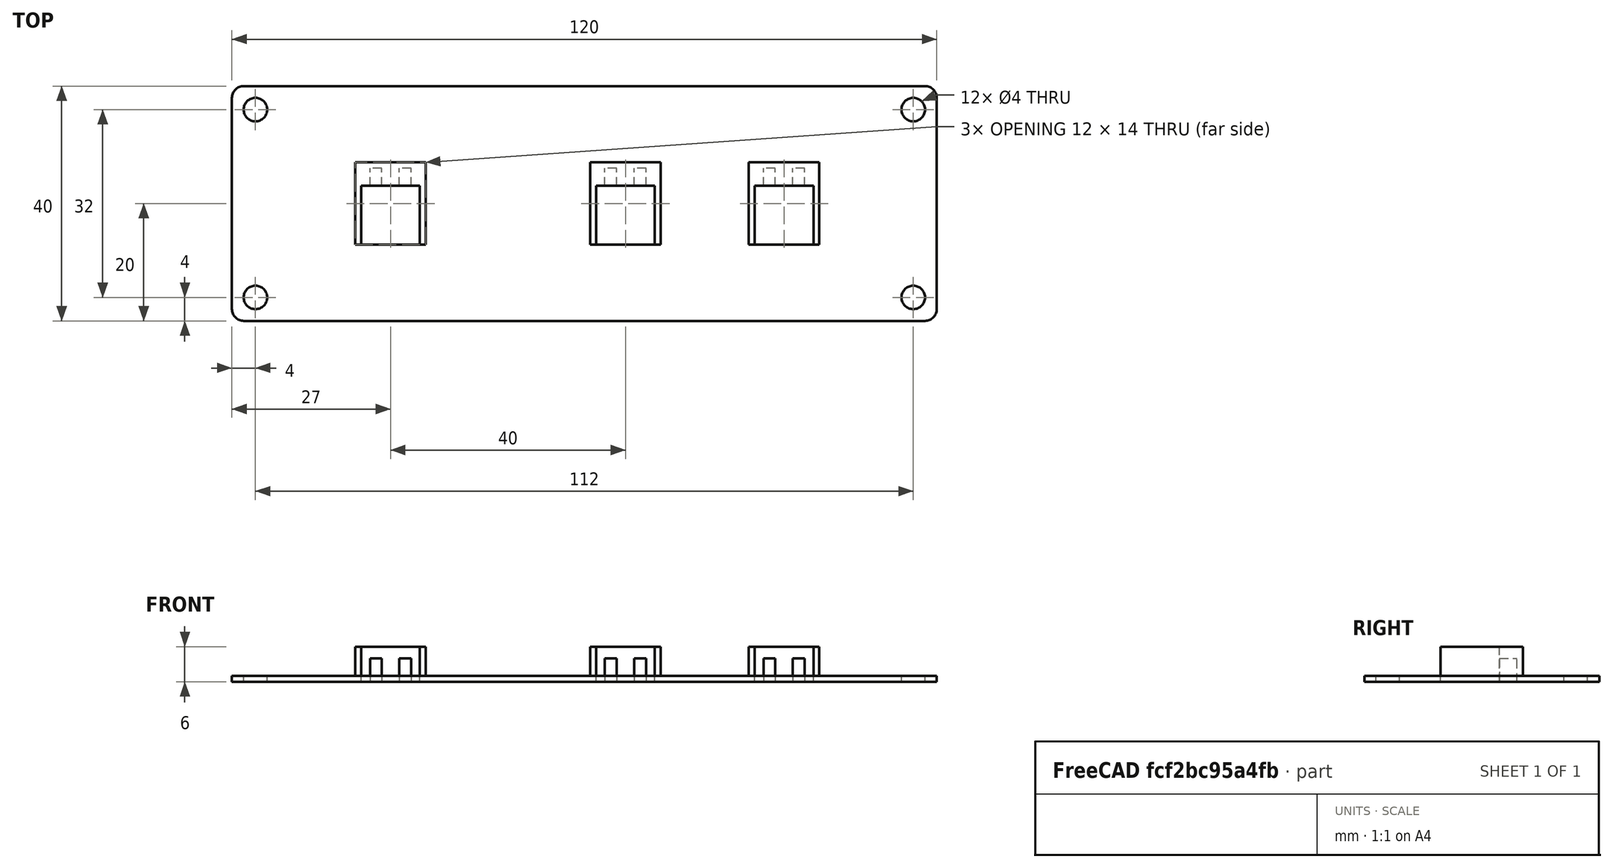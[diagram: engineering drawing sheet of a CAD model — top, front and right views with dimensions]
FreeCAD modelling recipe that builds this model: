
FCSTD DOCUMENT  (FreeCAD 0.18.4R)
Label: Parte_trasera
License: All rights reserved
LicenseURL: http://en.wikipedia.org/wiki/All_rights_reserved
objects: Part::Box×13, Part::MultiFuse×6, Part::Cut×2, Part::Feature×2, Part::Cylinder×1, Part::FeaturePython×1, Part::Fillet×1
note: 26 computed .brp shape members not serialized (recipe doc carries the construction recipe); baked Part::Feature solids carry a one-line shape summary decoded from their .brp

FEATURE [Part::Box] Box  label="Cubo"
  AttacherType = Attacher::AttachEngine3D
  Height = 1
  Length = 120
  Width = 40
FEATURE [Part::Cylinder] Cylinder  label="Cilindro"
  Angle = 360
  AttacherType = Attacher::AttachEngine3D
  Height = 10
  Placement = pos=(4,4,-1) rot=(0,0,1;0rad)
  Radius = 2
FEATURE [Part::FeaturePython] Array  # Draft array (typed FeaturePython)
  Angle = 360
  ArrayType = 0
  Axis = (0,0,1)
  Base = -> Cylinder
  Center = (0,0,0)
  Fuse = false
  IntervalAxis = (0,0,0)
  IntervalX = (112,0,0)
  IntervalY = (0,32,0)
  IntervalZ = (0,0,1)
  NumberPolar = 1
  NumberX = 2
  NumberY = 2
  NumberZ = 1
FEATURE [Part::Cut] Cut
  Base = -> Box
  Tool = -> Array
FEATURE [Part::Fillet] Fillet
  Base = -> Cut
  Edges = 4 edges r=2: [Edge1,Edge3,Edge6,Edge15]
FEATURE [Part::Feature] Fillet001
  shape: bbox 120 x 40 x 1 mm, 14 faces (baked)
FEATURE [Part::Box] Box001  label="Cubo001"
  AttacherType = Attacher::AttachEngine3D
  Height = 10
  Length = 10
  Width = 10
FEATURE [Part::Box] Box002  label="Cubo002"
  AttacherType = Attacher::AttachEngine3D
  Height = 10
  Length = 2
  Placement = pos=(1.5,3,-2) rot=(0,0,1;0rad)
  Width = 10
FEATURE [Part::Box] Box003  label="Cubo003"
  AttacherType = Attacher::AttachEngine3D
  Height = 10
  Length = 2
  Placement = pos=(6.5,3,-2) rot=(0,0,1;0rad)
  Width = 10
FEATURE [Part::Box] Box004  label="Cubo004"
  AttacherType = Attacher::AttachEngine3D
  Height = 6
  Length = 12
  Placement = pos=(-1,0,0) rot=(0,0,1;0rad)
  Width = 14
FEATURE [Part::MultiFuse] Fusion
  Placement = pos=(22,13,-4) rot=(0,0,1;0rad)
  Shapes = -> [Box001,Box002,Box003]
FEATURE [Part::Box] Box005  label="Cubo005"
  AttacherType = Attacher::AttachEngine3D
  Height = 6
  Length = 12
  Placement = pos=(39,0,0) rot=(0,0,1;0rad)
  Width = 14
FEATURE [Part::Box] Box006  label="Cubo006"
  AttacherType = Attacher::AttachEngine3D
  Height = 6
  Length = 12
  Placement = pos=(66,0,0) rot=(0,0,1;0rad)
  Width = 14
FEATURE [Part::MultiFuse] Fusion001
  Placement = pos=(22,13,0) rot=(0,0,1;0rad)
  Shapes = -> [Box004,Box005,Box006]
FEATURE [Part::MultiFuse] Fusion002
  Shapes = -> [Fillet,Fusion001]
FEATURE [Part::Box] Box007  label="Cubo007"
  AttacherType = Attacher::AttachEngine3D
  Height = 10
  Length = 2
  Placement = pos=(1.5,3,-2) rot=(0,0,1;0rad)
  Width = 10
FEATURE [Part::Box] Box008  label="Cubo008"
  AttacherType = Attacher::AttachEngine3D
  Height = 10
  Length = 10
  Width = 10
FEATURE [Part::Box] Box009  label="Cubo009"
  AttacherType = Attacher::AttachEngine3D
  Height = 10
  Length = 2
  Placement = pos=(6.5,3,-2) rot=(0,0,1;0rad)
  Width = 10
FEATURE [Part::MultiFuse] Fusion003
  Placement = pos=(62,13,-4) rot=(0,0,1;0rad)
  Shapes = -> [Box008,Box007,Box009]
FEATURE [Part::Box] Box010  label="Cubo010"
  AttacherType = Attacher::AttachEngine3D
  Height = 10
  Length = 2
  Placement = pos=(1.5,3,-2) rot=(0,0,1;0rad)
  Width = 10
FEATURE [Part::Box] Box011  label="Cubo011"
  AttacherType = Attacher::AttachEngine3D
  Height = 10
  Length = 10
  Width = 10
FEATURE [Part::Box] Box012  label="Cubo012"
  AttacherType = Attacher::AttachEngine3D
  Height = 10
  Length = 2
  Placement = pos=(6.5,3,-2) rot=(0,0,1;0rad)
  Width = 10
FEATURE [Part::MultiFuse] Fusion004
  Placement = pos=(89,13,-4) rot=(0,0,1;0rad)
  Shapes = -> [Box011,Box010,Box012]
FEATURE [Part::MultiFuse] Fusion005
  Shapes = -> [Fusion,Fusion003,Fusion004]
FEATURE [Part::Cut] Cut001
  Base = -> Fusion002
  Tool = -> Fusion005
FEATURE [Part::Feature] Cut001001  label="Cut002"
  shape: bbox 120 x 40 x 6 mm, 68 faces (baked)
